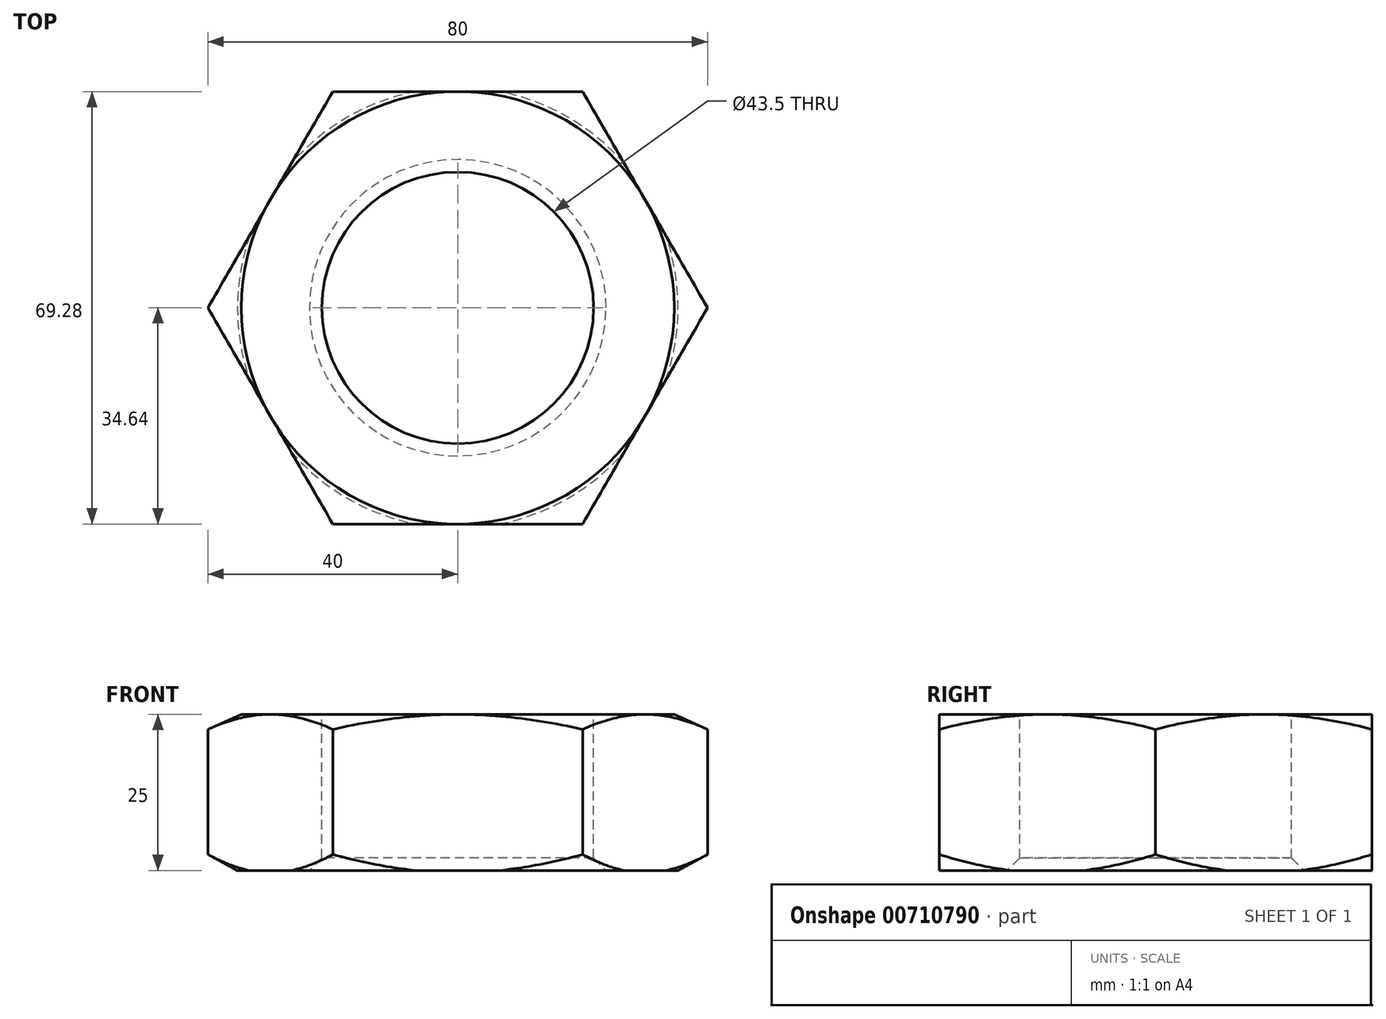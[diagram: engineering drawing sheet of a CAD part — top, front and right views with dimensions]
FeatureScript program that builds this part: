
annotation { "Feature Type Name" : "Feature", "Feature Type Description" : "" }
export const myFeature = defineFeature(function(context is Context, id is Id, definition is map)
    precondition{}
    {
        {
            var Q0;
            Q0=qCreatedBy(makeId("Top.planeOp"),FACE);
            var sketch = newSketch(context, id + "F0", { "sketchPlane" : qUnion([Q0])});
            skCircle(sketch, "E0.cCircle", {"center": v(0, 0) * mm, "radius": 34.64 * mm, "construction": true});
            skLineSegment(sketch, "E0.0", {"start": v(-20, 34.64) * mm, "end": v(20, 34.64) * mm});
            skLineSegment(sketch, "E0.1", {"start": v(20, 34.64) * mm, "end": v(40, 0) * mm});
            skLineSegment(sketch, "E0.2", {"start": v(40, 0) * mm, "end": v(20, -34.64) * mm});
            skLineSegment(sketch, "E0.3", {"start": v(20, -34.64) * mm, "end": v(-20, -34.64) * mm});
            skLineSegment(sketch, "E0.4", {"start": v(-20, -34.64) * mm, "end": v(-40, 0) * mm});
            skLineSegment(sketch, "E0.5", {"start": v(-40, 0) * mm, "end": v(-20, 34.64) * mm});
            skPoint(sketch, "E0.0.midPoint", {"position": v(0, 34.64) * mm});
            skSolve(sketch);
        }
        {
            var Q0;
            Q0=makeQuery(id+"F0.imprint","IMPRINT",FACE,{"disambiguationData":[TD([[makeQuery(id+"F0.imprint","IMPRINT",EDGE,{"derivedFrom":sQuery(id+"F0.wireOp",EDGE,"E0.0")}),-1.0]])]});
            extrude(context, id + "F1", {"entities" : qUnion([Q0]), "depth" : 25 * mm, "offsetDistance" : 25 * mm});
        }
        {
            var Q0;
            Q0=makeQuery(id+"F1.opExtrude","CAP_FACE",FACE,{"disambiguationData":[OSD([sQuery(id+"F0.wireOp",EDGE,"E0.0"),sQuery(id+"F0.wireOp",EDGE,"E0.1"),sQuery(id+"F0.wireOp",EDGE,"E0.2"),sQuery(id+"F0.wireOp",EDGE,"E0.3"),sQuery(id+"F0.wireOp",EDGE,"E0.4"),sQuery(id+"F0.wireOp",EDGE,"E0.5")])],"isStart":false});
            var sketch = newSketch(context, id + "F2", { "sketchPlane" : qUnion([Q0])});
            skCircle(sketch, "E1", {"center": v(0, 0) * mm, "radius": 21.75 * mm});
            skSolve(sketch);
        }
        {
            var Q0;
            Q0=makeQuery(id+"F2.imprint","IMPRINT",FACE,{"disambiguationData":[TD([[makeQuery(id+"F2.imprint","IMPRINT",EDGE,{"derivedFrom":sQuery(id+"F2.wireOp",EDGE,"E1")}),1.0]])]});
            extrude(context, id + "F3", {"entities" : qUnion([Q0]), "operationType" : NewBodyOperationType.REMOVE, "endBound" : BoundingType.THROUGH_ALL, "oppositeDirection" : true, "depth" : 25 * mm, "offsetDistance" : 25 * mm});
        }
        {
            var Q0;
            Q0=makeQuery(id+"F3.boolean.opBoolean","INTERSECT",EDGE,{"derivedFrom":[makeQuery(id+"F1.opExtrude","CAP_FACE",FACE,{"disambiguationData":[OSD([sQuery(id+"F0.wireOp",EDGE,"E0.0"),sQuery(id+"F0.wireOp",EDGE,"E0.1"),sQuery(id+"F0.wireOp",EDGE,"E0.2"),sQuery(id+"F0.wireOp",EDGE,"E0.3"),sQuery(id+"F0.wireOp",EDGE,"E0.4"),sQuery(id+"F0.wireOp",EDGE,"E0.5")])],"isStart":true}),makeQuery(id+"F3.opExtrude","SWEPT_FACE",FACE,{"disambiguationData":[OSD([sQuery(id+"F2.wireOp",EDGE,"E1")])]})]});
            var Q1;
            Q1=makeQuery(id+"F3.boolean.opBoolean","COPY",EDGE,{"derivedFrom":makeQuery(id+"F3.opExtrude","CAP_EDGE",EDGE,{"disambiguationData":[OSD([sQuery(id+"F2.wireOp",EDGE,"E1")])],"isStart":true})});
            chamfer(context, id + "F4", {"entities" : qUnion([Q0, Q1]), "width" : 2 * mm, "tangentPropagation" : true});
        }
        {
            var Q0;
            Q0=qCreatedBy(makeId("Front.planeOp"),FACE);
            var sketch = newSketch(context, id + "F5", { "sketchPlane" : qUnion([Q0])});
            skLineSegment(sketch, "E2", {"start": v(33.52, 25.5) * mm, "end": v(42.4, 21.53) * mm});
            skLineSegment(sketch, "E3", {"start": v(42.4, 21.53) * mm, "end": v(42.4, 25.5) * mm});
            skLineSegment(sketch, "E4", {"start": v(42.4, 25.5) * mm, "end": v(33.52, 25.5) * mm});
            skLineSegment(sketch, "E5", {"start": v(33.52, -0.95) * mm, "end": v(42.14, 3.73) * mm});
            skLineSegment(sketch, "E6", {"start": v(42.14, 3.73) * mm, "end": v(42.14, -0.95) * mm});
            skLineSegment(sketch, "E7", {"start": v(42.14, -0.95) * mm, "end": v(33.52, -0.95) * mm});
            skLineSegment(sketch, "E8", {"start": v(0, 49.49) * mm, "end": v(0, -33.66) * mm, "construction": true});
            skSolve(sketch);
        }
        {
            var Q0;
            Q0=makeQuery(id+"F5.imprint","IMPRINT",FACE,{"disambiguationData":[TD([[makeQuery(id+"F5.imprint","IMPRINT",EDGE,{"derivedFrom":sQuery(id+"F5.wireOp",EDGE,"E2")}),1.0]])]});
            var Q1;
            Q1=makeQuery(id+"F5.imprint","IMPRINT",FACE,{"disambiguationData":[TD([[makeQuery(id+"F5.imprint","IMPRINT",EDGE,{"derivedFrom":sQuery(id+"F5.wireOp",EDGE,"E5")}),-1.0]])]});
            var Q2;
            Q2=sQuery(id+"F5.wireOp",EDGE,"E8");
            revolve(context, id + "F6", {"operationType" : NewBodyOperationType.REMOVE, "surfaceOperationType" : NewSurfaceOperationType.NEW, "entities" : qUnion([Q0, Q1]), "axis" : qUnion([Q2]), "revolveType" : RevolveType.FULL, "oppositeDirection" : true});
        }
    });
